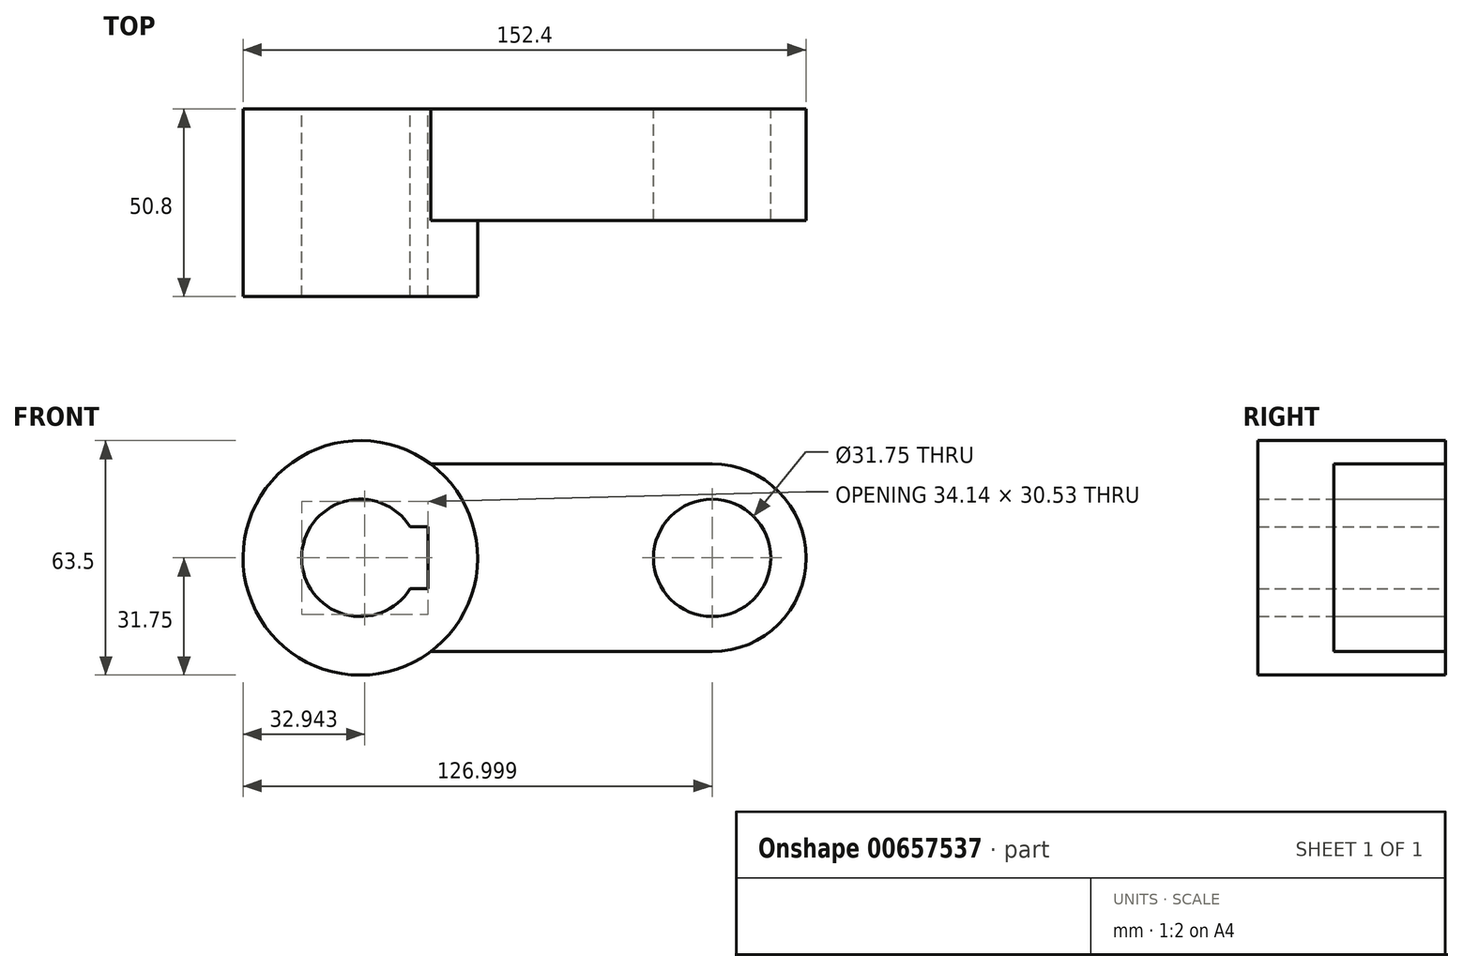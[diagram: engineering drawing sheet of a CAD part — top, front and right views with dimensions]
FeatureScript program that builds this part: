
annotation { "Feature Type Name" : "Feature", "Feature Type Description" : "" }
export const myFeature = defineFeature(function(context is Context, id is Id, definition is map)
    precondition{}
    {
        {
            var Q0;
            Q0=qCreatedBy(makeId("Front.planeOp"),FACE);
            var sketch = newSketch(context, id + "F0", { "sketchPlane" : qUnion([Q0])});
            skLineSegment(sketch, "E0", {"start": v(-51.87, 0) * mm, "end": v(24.33, 0) * mm});
            skArc(sketch, "E1", {"start": v(24.33, 0) * mm, "mid": v(49.73, 25.4) * mm, "end": v(24.33, 50.8) * mm});
            skLineSegment(sketch, "E2", {"start": v(24.33, 50.8) * mm, "end": v(-51.87, 50.8) * mm});
            skCircle(sketch, "E3", {"center": v(-70.92, 25.4) * mm, "radius": 31.75 * mm});
            skCircle(sketch, "E4", {"center": v(24.33, 25.4) * mm, "radius": 15.88 * mm});
            skCircle(sketch, "E5", {"center": v(24.33, 25.4) * mm, "radius": 9.53 * mm});
            skArc(sketch, "E6", {"start": v(-58.22, 34.93) * mm, "mid": v(-86.8, 25.4) * mm, "end": v(-58.22, 15.87) * mm});
            skLineSegment(sketch, "E7.bottom", {"start": v(-50.28, 34.92) * mm, "end": v(-58.22, 34.92) * mm});
            skLineSegment(sketch, "E7.top", {"start": v(-50.28, 15.88) * mm, "end": v(-58.22, 15.88) * mm});
            skLineSegment(sketch, "E7.left", {"start": v(-50.28, 34.92) * mm, "end": v(-50.28, 15.88) * mm});
            skPoint(sketch, "E7.middle", {"position": v(-55.05, 25.4) * mm});
            skPoint(sketch, "E8.orphan", {"position": v(-59.8, 34.92) * mm});
            skPoint(sketch, "E9.orphan", {"position": v(-59.8, 15.88) * mm});
            skSolve(sketch);
        }
        {
            var Q0;
            {var subQ1=sQuery(id+"F0.wireOp",EDGE,"E0");Q0=makeQuery(id+"F0.imprint","IMPRINT",FACE,{"disambiguationData":[TD([[makeQuery(id+"F0.imprint","IMPRINT",EDGE,{"derivedFrom":subQ1}),1.0]])]});}
            extrude(context, id + "F1", {"entities" : qUnion([Q0]), "depth" : 30.18 * mm, "offsetDistance" : 25.4 * mm});
        }
        {
            var Q0;
            Q0=qCreatedBy(makeId("Front.planeOp"),FACE);
            var sketch = newSketch(context, id + "F2", { "sketchPlane" : qUnion([Q0])});
            skCircle(sketch, "E10", {"center": v(-70.92, 25.4) * mm, "radius": 31.75 * mm});
            skArc(sketch, "E11", {"start": v(-57.43, 33.77) * mm, "mid": v(-86.8, 25.4) * mm, "end": v(-57.43, 17.03) * mm});
            skLineSegment(sketch, "E12.bottom", {"start": v(-52.66, 33.77) * mm, "end": v(-57.43, 33.77) * mm});
            skLineSegment(sketch, "E12.top", {"start": v(-52.66, 17.03) * mm, "end": v(-57.43, 17.03) * mm});
            skLineSegment(sketch, "E12.left", {"start": v(-52.66, 33.77) * mm, "end": v(-52.66, 17.03) * mm});
            skPoint(sketch, "E12.middle", {"position": v(-55.05, 25.4) * mm});
            skSolve(sketch);
        }
        {
            var Q0;
            Q0=makeQuery(id+"F2.imprint","IMPRINT",FACE,{"disambiguationData":[TD([[makeQuery(id+"F2.imprint","IMPRINT",EDGE,{"derivedFrom":sQuery(id+"F2.wireOp",EDGE,"E10")}),1.0]])]});
            extrude(context, id + "F3", {"entities" : qUnion([Q0]), "operationType" : NewBodyOperationType.ADD, "depth" : 50.8 * mm, "offsetDistance" : 25.4 * mm});
        }
    });
